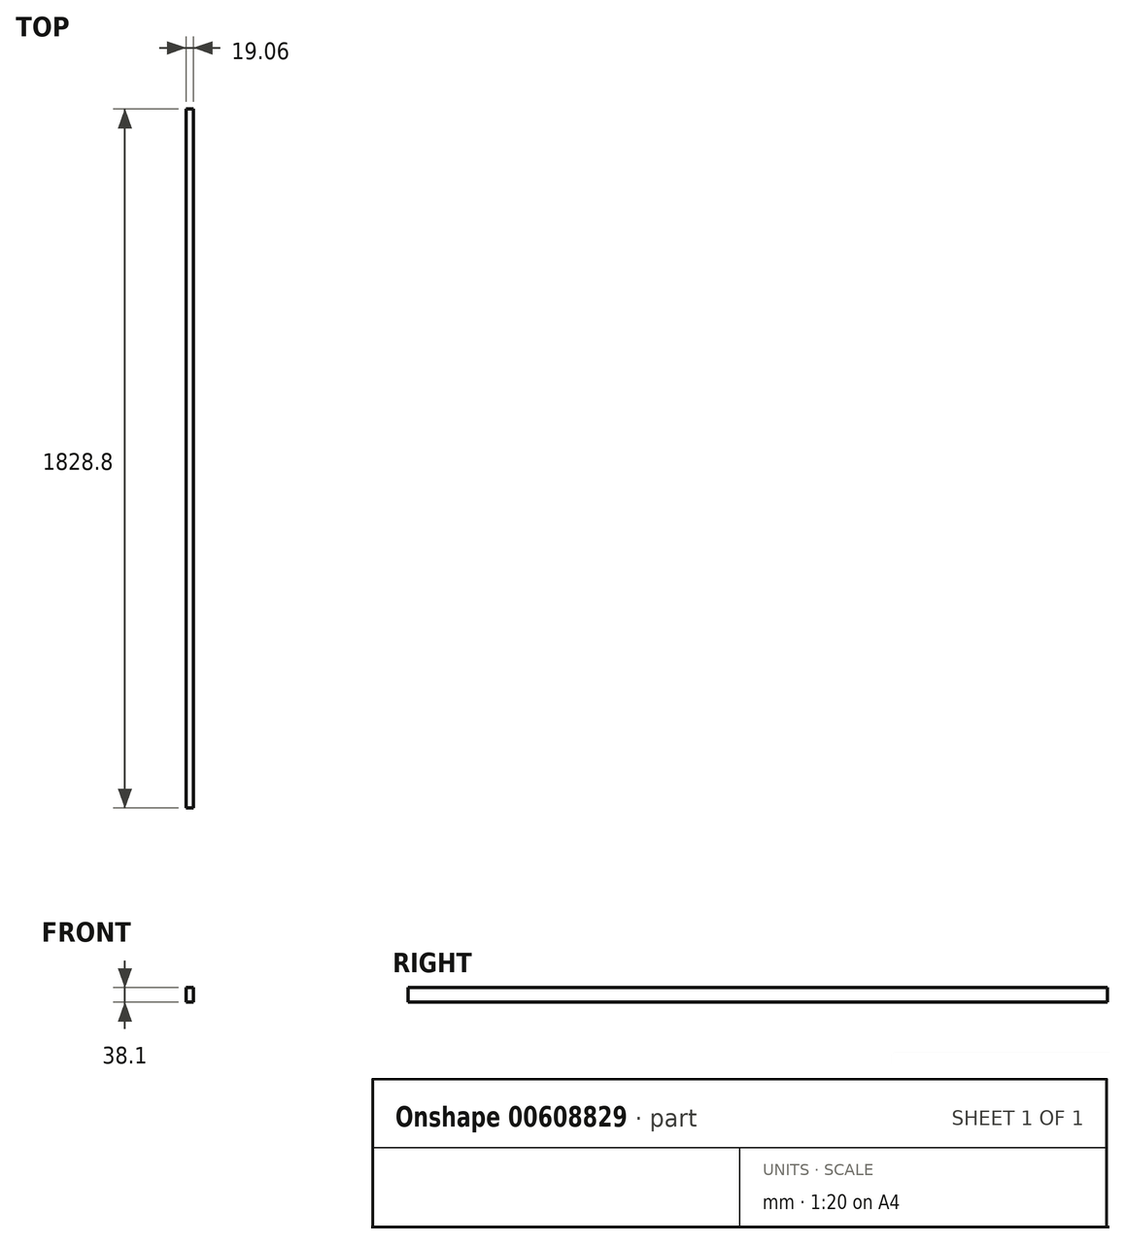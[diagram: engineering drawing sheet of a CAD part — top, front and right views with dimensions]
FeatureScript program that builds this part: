
annotation { "Feature Type Name" : "Feature", "Feature Type Description" : "" }
export const myFeature = defineFeature(function(context is Context, id is Id, definition is map)
    precondition{}
    {
        {
            var Q0;
            Q0=qCreatedBy(makeId("Front.planeOp"),FACE);
            var sketch = newSketch(context, id + "F0", { "sketchPlane" : qUnion([Q0])});
            skLineSegment(sketch, "E0.bottom", {"start": v(9.52, 19.05) * mm, "end": v(-9.53, 19.05) * mm});
            skLineSegment(sketch, "E0.top", {"start": v(9.53, -19.05) * mm, "end": v(-9.52, -19.05) * mm});
            skLineSegment(sketch, "E0.left", {"start": v(9.52, 19.05) * mm, "end": v(9.53, -19.05) * mm});
            skLineSegment(sketch, "E0.right", {"start": v(-9.53, 19.05) * mm, "end": v(-9.52, -19.05) * mm});
            skPoint(sketch, "E0.middle", {"position": v(0, 0) * mm});
            skSolve(sketch);
        }
        {
            var Q0;
            Q0=qSketchRegion(id+"F0",true);
            extrude(context, id + "F1", {"entities" : qUnion([Q0]), "endBound" : BoundingType.SYMMETRIC, "depth" : 1828.8 * mm, "offsetDistance" : 25.4 * mm});
        }
    });
